# Revit family: Birka Bench
name_source: partatom
category: Furniture
units: mm (PartAtom-declared; Revit-internal decimal feet)

## family parameters
Always vertical = Yes
Cut with Voids When Loaded = No
OmniClass Number = 23.21.23.13.15
Room Calculation Point = No
Shared = No
Work Plane-Based = No

## types (4) — shared parameters
BIM Category = Bench & Park Bench
Description = Park Bench Birka
Edition number = 1
IFC Classification = Furniture
Manufacturer = Hags
Manufacturer name = HAGS
OmniClass Code = 23-21 23 13 15
OmniClass Description = Residential Sofas
Product Guid = 90e49432-c870-4a59-897e-b15016e8f9bd
Product data url = https://www.bimobject.com
Product name = Park Bench Birka
Product url = https://hags.co.uk
URL = https://www.hags.com
Uniclass 1.4 Code = L8211
Uniclass 1.4 Description = Furniture
zero-valued in all types: Default Elevation

## per-type parameters (varying)
| type | Body material | Body material_90 | Construction material | Model |
| 8037715 Bark Borwn / Black | Hags - Wood - Bark brown | Hags - Wood - Bark brown 90 | Hags - Steel - Powder coated - Black | 8037715 |
| 8037716 Bark Borwn / Galvanized | Hags - Wood - Bark brown | Hags - Wood - Bark brown 90 | Hags - Steel - Galvanized | 8037716 |
| 8003213 Red pine / Galvanized | Hags - Red Pine Wood | Hags - Red Pine Wood | Hags - Steel - Galvanized | 8003213 |
| 8003218 Hardwood / Galvanized | Hags - Hard Wood | Hags - Hard Wood | Hags - Steel - Galvanized | 8003213 |

## geometry (parser evidence)
native form markers: Sweep x2
no freeform markers — native parametric forms only
